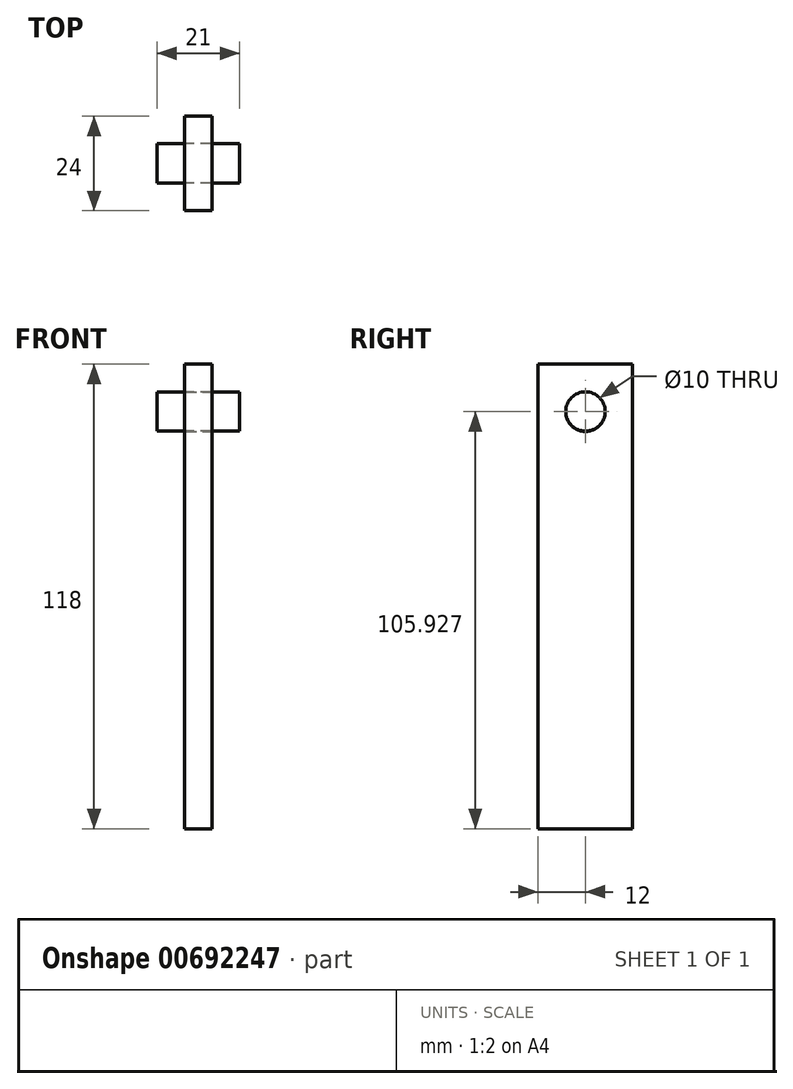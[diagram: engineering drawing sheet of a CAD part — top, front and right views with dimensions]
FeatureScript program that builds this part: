
annotation { "Feature Type Name" : "Feature", "Feature Type Description" : "" }
export const myFeature = defineFeature(function(context is Context, id is Id, definition is map)
    precondition{}
    {
        {
            var Q0;
            Q0=qCreatedBy(makeId("Top.planeOp"),FACE);
            var sketch = newSketch(context, id + "F0", { "sketchPlane" : qUnion([Q0])});
            skLineSegment(sketch, "E0.bottom", {"start": v(-3.5, 12) * mm, "end": v(3.5, 12) * mm});
            skLineSegment(sketch, "E0.top", {"start": v(-3.5, -12) * mm, "end": v(3.5, -12) * mm});
            skLineSegment(sketch, "E0.left", {"start": v(-3.5, 12) * mm, "end": v(-3.5, -12) * mm});
            skLineSegment(sketch, "E0.right", {"start": v(3.5, 12) * mm, "end": v(3.5, -12) * mm});
            skSolve(sketch);
        }
        {
            var Q0;
            Q0 = qSketchRegion(id + "F0", true);
            extrude(context, id + "F1", {"entities" : qUnion([Q0]), "depth" : 118 * mm, "offsetDistance" : 25 * mm});
        }
        {
            var Q0;
            Q0=makeQuery(id+"F1.opExtrude","SWEPT_FACE",FACE,{"disambiguationData":[OSD([sQuery(id+"F0.wireOp",EDGE,"E0.right")])]});
            var sketch = newSketch(context, id + "F2", { "sketchPlane" : qUnion([Q0])});
            skCircle(sketch, "E1", {"center": v(0, 105.93) * mm, "radius": 5 * mm});
            skSolve(sketch);
        }
        {
            var Q0;
            Q0=makeQuery(id+"F2.imprint","IMPRINT",FACE,{"disambiguationData":[TD([[makeQuery(id+"F2.imprint","IMPRINT",EDGE,{"derivedFrom":sQuery(id+"F2.wireOp",EDGE,"E1")}),1.0]])]});
            extrude(context, id + "F3", {"entities" : qUnion([Q0]), "operationType" : NewBodyOperationType.REMOVE, "oppositeDirection" : true, "depth" : 25 * mm, "offsetDistance" : 25 * mm});
        }
        {
            var Q0;
            Q0=qCreatedBy(makeId("Right.planeOp"),FACE);
            var sketch = newSketch(context, id + "F4", { "sketchPlane" : qUnion([Q0])});
            skCircle(sketch, "E2", {"center": v(0, 106) * mm, "radius": 5 * mm});
            skSolve(sketch);
        }
        {
            var Q0;
            Q0 = qSketchRegion(id + "F4", true);
            extrude(context, id + "F5", {"entities" : qUnion([Q0]), "depth" : 21 * mm, "offsetDistance" : 25 * mm});
        }
        {
            var Q0;
            Q0=makeQuery(id+"F5.opExtrude","SWEPT_BODY",BODY,{"disambiguationData":[OSD([sQuery(id+"F4.wireOp",EDGE,"E2")])]});
            var Q1;
            Q1=makeQuery(id+"F5.opExtrude","SWEPT_FACE",FACE,{"disambiguationData":[OSD([sQuery(id+"F4.wireOp",EDGE,"E2")])]});
            transform(context, id + "F6", {"entities" : qUnion([Q0]), "transformType" : TransformType.TRANSLATION_DISTANCE, "transformDirection" : qUnion([Q1]), "distance" : 10.5 * mm, "makeCopy" : false});
        }
    });
